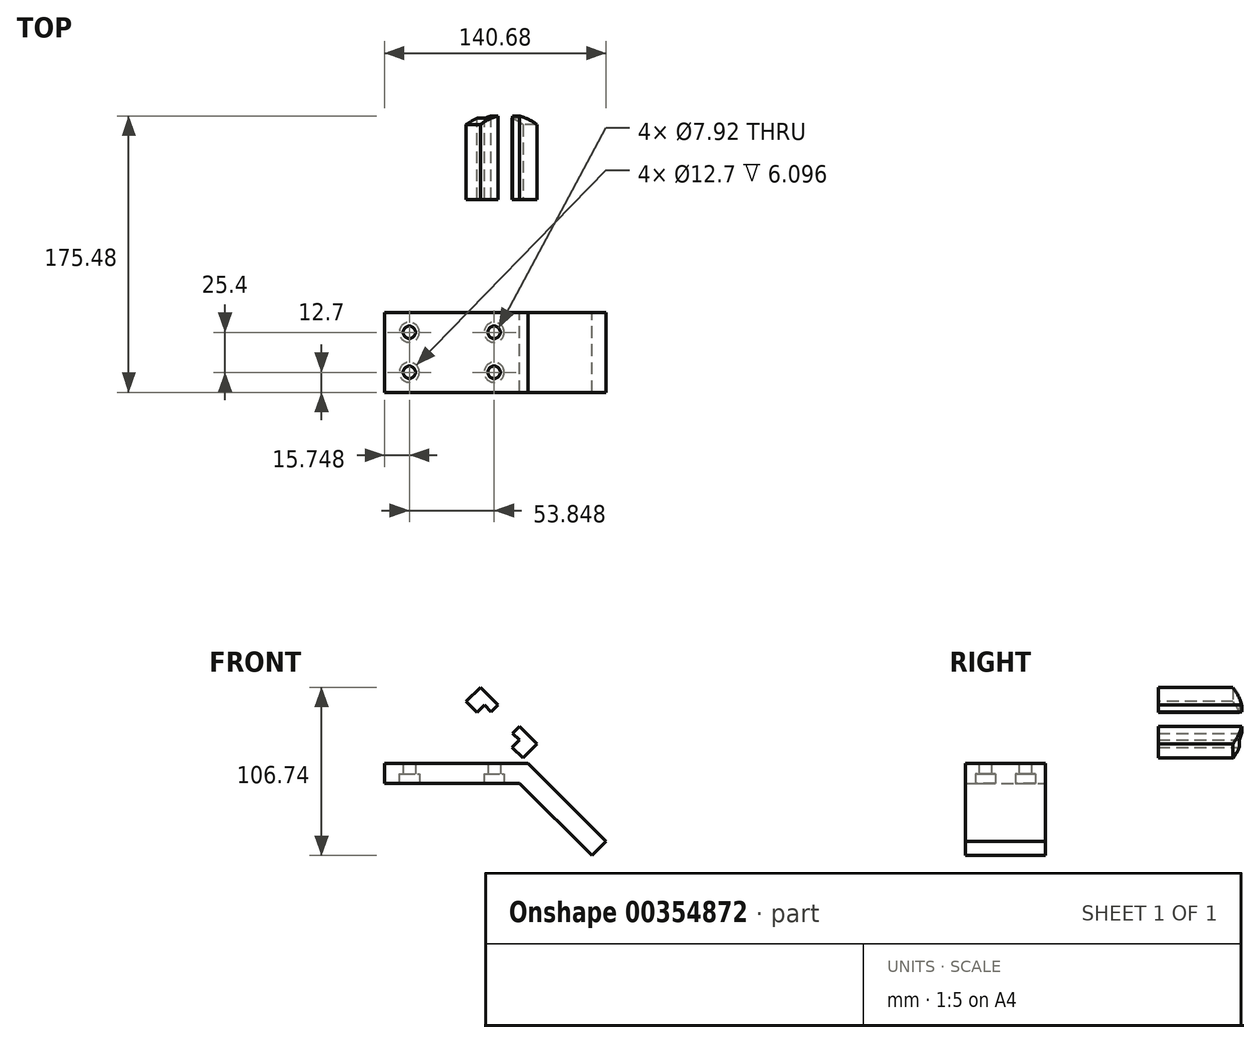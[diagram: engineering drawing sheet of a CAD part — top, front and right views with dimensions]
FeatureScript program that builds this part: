
annotation { "Feature Type Name" : "Feature", "Feature Type Description" : "" }
export const myFeature = defineFeature(function(context is Context, id is Id, definition is map)
    precondition{}
    {
        {
            var Q0;
            Q0=qCreatedBy(makeId("Front.planeOp"),FACE);
            var sketch = newSketch(context, id + "F0", { "sketchPlane" : qUnion([Q0])});
            skLineSegment(sketch, "E0", {"start": v(0, 0) * mm, "end": v(85.85, 0) * mm});
            skLineSegment(sketch, "E1", {"start": v(85.85, 0) * mm, "end": v(131.7, -45.85) * mm});
            skLineSegment(sketch, "E2", {"start": v(131.7, -45.85) * mm, "end": v(140.68, -36.87) * mm});
            skLineSegment(sketch, "E3", {"start": v(140.68, -36.87) * mm, "end": v(91.11, 12.7) * mm});
            skLineSegment(sketch, "E4", {"start": v(91.11, 12.7) * mm, "end": v(0, 12.7) * mm});
            skLineSegment(sketch, "E5", {"start": v(0, 12.7) * mm, "end": v(0, 0) * mm});
            skSolve(sketch);
        }
        {
            var Q0;
            Q0 = qSketchRegion(id + "F0", true);
            extrude(context, id + "F1", {"entities" : qUnion([Q0]), "depth" : 50.8 * mm});
        }
        {
            var Q0;
            Q0=makeQuery(id+"F1.opExtrude","SWEPT_FACE",FACE,{"disambiguationData":[OSD([sQuery(id+"F0.wireOp",EDGE,"E4")])]});
            var sketch = newSketch(context, id + "F2", { "sketchPlane" : qUnion([Q0])});
            skLineSegment(sketch, "E6", {"start": v(15.75, 0) * mm, "end": v(15.75, -50.8) * mm, "construction": true});
            skLineSegment(sketch, "E7", {"start": v(69.6, 0) * mm, "end": v(69.6, -50.8) * mm, "construction": true});
            skLineSegment(sketch, "E8", {"start": v(0, -12.7) * mm, "end": v(91.11, -12.7) * mm, "construction": true});
            skLineSegment(sketch, "E9", {"start": v(0, -38.1) * mm, "end": v(91.11, -38.1) * mm, "construction": true});
            skPoint(sketch, "E10", {"position": v(15.75, -12.7) * mm});
            skPoint(sketch, "E11", {"position": v(69.6, -12.7) * mm});
            skPoint(sketch, "E12", {"position": v(69.6, -38.1) * mm});
            skPoint(sketch, "E13", {"position": v(15.75, -38.1) * mm});
            skSolve(sketch);
        }
        {
            var Q0;
            Q0=makeQuery(id+"F1.opExtrude","SWEPT_FACE",FACE,{"disambiguationData":[OSD([sQuery(id+"F0.wireOp",EDGE,"E0")])]});
            var sketch = newSketch(context, id + "F3", { "sketchPlane" : qUnion([Q0])});
            skPoint(sketch, "E14.0", {"position": v(15.75, 38.1) * mm});
            skPoint(sketch, "E15.0", {"position": v(15.75, 12.7) * mm});
            skPoint(sketch, "E16.0", {"position": v(69.6, 38.1) * mm});
            skPoint(sketch, "E17.0", {"position": v(69.6, 12.7) * mm});
            skSolve(sketch);
        }
        {
            var Q0;
            Q0=sQuery(id+"F3.wireOp",VERTEX,"E14.0");
            var Q1;
            Q1=sQuery(id+"F3.wireOp",VERTEX,"E16.0");
            var Q2;
            Q2=sQuery(id+"F3.wireOp",VERTEX,"E17.0");
            var Q3;
            Q3=sQuery(id+"F3.wireOp",VERTEX,"E15.0");
            var Q4;
            Q4=makeQuery(id+"F1.opExtrude","SWEPT_BODY",BODY,{"disambiguationData":[OSD([sQuery(id+"F0.wireOp",EDGE,"E0"),sQuery(id+"F0.wireOp",EDGE,"E1"),sQuery(id+"F0.wireOp",EDGE,"E2"),sQuery(id+"F0.wireOp",EDGE,"E3"),sQuery(id+"F0.wireOp",EDGE,"E4"),sQuery(id+"F0.wireOp",EDGE,"E5")])]});
            hole(context, id + "F4", {"style" : HoleStyle.C_BORE, "endStyle" : HoleEndStyle.BLIND, "holeDiameter" : 7.92 * mm, "cBoreDiameter" : 12.7 * mm, "cBoreDepth" : 6.1 * mm, "holeDepth" : 35.56 * mm, "isTappedThrough" : true, "tappedDepth" : 12.7 * mm, "tapClearance" : 3, "startFromSketch" : true, "locations" : qUnion([Q0, Q1, Q2, Q3]), "scope" : qUnion([Q4])});
        }
        {
            var Q0;
            Q0=makeQuery(id+"F1.opExtrude","SWEPT_FACE",FACE,{"disambiguationData":[OSD([sQuery(id+"F0.wireOp",EDGE,"E3")])]});
            var sketch = newSketch(context, id + "F5", { "sketchPlane" : qUnion([Q0])});
            skLineSegment(sketch, "E18", {"start": v(71.7, -50.8) * mm, "end": v(71.7, 0) * mm, "construction": true});
            skArc(sketch, "E19", {"start": v(71.7, -79.25) * mm, "mid": v(125.55, -25.83) * mm, "end": v(72.56, 28.44) * mm});
            skPoint(sketch, "E19.startSnap0", {"position": v(71.7, -25.4) * mm});
            skLineSegment(sketch, "E20.0", {"start": v(125.55, -50.8) * mm, "end": v(55.45, -50.8) * mm});
            skLineSegment(sketch, "E21.0", {"start": v(125.55, 0) * mm, "end": v(55.45, 0) * mm});
            skLineSegment(sketch, "E22.0", {"start": v(125.55, -50.8) * mm, "end": v(125.55, 0) * mm});
            skSolve(sketch);
        }
        {
            var Q0;
            {var subQ0=sQuery(id+"F5.wireOp",EDGE,"E20.0");var subQ1=sQuery(id+"F5.wireOp",EDGE,"E19");var subQ2=makeQuery(id+"F5.imprint","INTERSECT",VERTEX,{"derivedFrom":[subQ1,subQ0]});Q0=makeQuery(id+"F5.imprint","IMPRINT",FACE,{"disambiguationData":[TD([[makeQuery(id+"F5.imprint","IMPRINT",EDGE,{"disambiguationData":[TD([[subQ2,-1.0]])],"derivedFrom":subQ1}),-1.0]])]});}
            var Q1;
            {var subQ0=sQuery(id+"F5.wireOp",EDGE,"E21.0");var subQ1=sQuery(id+"F5.wireOp",EDGE,"E19");var subQ2=makeQuery(id+"F5.imprint","INTERSECT",VERTEX,{"derivedFrom":[subQ1,subQ0]});Q1=makeQuery(id+"F5.imprint","IMPRINT",FACE,{"disambiguationData":[TD([[makeQuery(id+"F5.imprint","IMPRINT",EDGE,{"disambiguationData":[TD([[subQ2,1.0]])],"derivedFrom":subQ1}),-1.0]])]});}
            extrude(context, id + "F6", {"entities" : qUnion([Q0, Q1]), "operationType" : NewBodyOperationType.REMOVE, "endBound" : BoundingType.THROUGH_ALL, "oppositeDirection" : true, "depth" : 25.4 * mm});
        }
        {
            var Q0;
            Q0=makeQuery(id+"F1.opExtrude","SWEPT_FACE",FACE,{"disambiguationData":[OSD([sQuery(id+"F0.wireOp",EDGE,"E3")])]});
            var sketch = newSketch(context, id + "F7", { "sketchPlane" : qUnion([Q0])});
            skLineSegment(sketch, "E23", {"start": v(71.7, -50.8) * mm, "end": v(71.7, 0) * mm});
            skLineSegment(sketch, "E24", {"start": v(71.7, -35.05) * mm, "end": v(124.68, -35.05) * mm});
            skLineSegment(sketch, "E25", {"start": v(71.7, -15.75) * mm, "end": v(124.68, -15.75) * mm});
            skLineSegment(sketch, "E26.0", {"start": v(119.18, -50.8) * mm, "end": v(55.45, -50.8) * mm});
            skArc(sketch, "E27.0", {"start": v(119.18, -50.8) * mm, "mid": v(125.55, -25.4) * mm, "end": v(119.18, 0) * mm});
            skLineSegment(sketch, "E28.0", {"start": v(119.18, 0) * mm, "end": v(55.45, 0) * mm});
            skLineSegment(sketch, "E29", {"start": v(71.7, -41.15) * mm, "end": v(123.2, -41.15) * mm});
            skLineSegment(sketch, "E30", {"start": v(71.7, -9.65) * mm, "end": v(123.2, -9.65) * mm});
            skSolve(sketch);
        }
        {
            var Q0;
            {var subQ3=sQuery(id+"F7.wireOp",EDGE,"E29");Q0=makeQuery(id+"F7.imprint","IMPRINT",FACE,{"disambiguationData":[TD([[makeQuery(id+"F7.imprint","IMPRINT",EDGE,{"derivedFrom":subQ3}),-1.0]])]});}
            var Q1;
            {var subQ3=sQuery(id+"F7.wireOp",EDGE,"E30");Q1=makeQuery(id+"F7.imprint","IMPRINT",FACE,{"disambiguationData":[TD([[makeQuery(id+"F7.imprint","IMPRINT",EDGE,{"derivedFrom":subQ3}),1.0]])]});}
            var Q2;
            {var subQ0=sQuery(id+"F7.wireOp",EDGE,"E24");Q2=makeQuery(id+"F7.imprint","IMPRINT",FACE,{"disambiguationData":[TD([[makeQuery(id+"F7.imprint","IMPRINT",EDGE,{"derivedFrom":subQ0}),-1.0]])]});}
            var Q3;
            {var subQ0=sQuery(id+"F7.wireOp",EDGE,"E25");Q3=makeQuery(id+"F7.imprint","IMPRINT",FACE,{"disambiguationData":[TD([[makeQuery(id+"F7.imprint","IMPRINT",EDGE,{"derivedFrom":subQ0}),1.0]])]});}
            extrude(context, id + "F8", {"entities" : qUnion([Q0, Q1, Q2, Q3]), "operationType" : NewBodyOperationType.ADD, "depth" : 12.7 * mm});
        }
        {
            var Q0;
            {var subQ0=sQuery(id+"F7.wireOp",EDGE,"E24");Q0=makeQuery(id+"F7.imprint","IMPRINT",FACE,{"disambiguationData":[TD([[makeQuery(id+"F7.imprint","IMPRINT",EDGE,{"derivedFrom":subQ0}),-1.0]])]});}
            var Q1;
            {var subQ0=sQuery(id+"F7.wireOp",EDGE,"E25");Q1=makeQuery(id+"F7.imprint","IMPRINT",FACE,{"disambiguationData":[TD([[makeQuery(id+"F7.imprint","IMPRINT",EDGE,{"derivedFrom":subQ0}),1.0]])]});}
            extrude(context, id + "F9", {"entities" : qUnion([Q0, Q1]), "operationType" : NewBodyOperationType.REMOVE, "depth" : 6.6 * mm});
        }
    });
